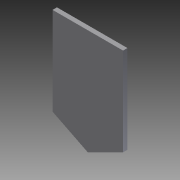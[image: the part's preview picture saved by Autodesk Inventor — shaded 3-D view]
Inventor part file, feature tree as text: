
AUTODESK INVENTOR PART (.ipt)
format: ipt  version: 2012 (Build 160160000, 160)  size: 67,072 bytes
history: native  units: in
note: dims shown in document units (in); Inventor stores cm internally (conversion verified against a paired STEP export)
features: extrude x1, sketch x1
ambient origin geometry x8: Origin, YZ Plane, XZ Plane, XY Plane, X Axis, Y Axis, Z Axis, Center Point
bodies: Solid1 (feature_tree)
feature tree (2):
  extrude  "Extrusion1"  Depth=3.0in
  sketch  "Sketch1"  dims[d0=2.0in d1=3.0in d2=2.5in d3=0.125in d4=0.0in]
